# Revit family: 201_RINO-V-_
name_source: partatom
category: Air Terminals
units: mm (PartAtom-declared; Revit-internal decimal feet)

## family parameters
Always vertical = Yes
Cut with Voids When Loaded = No
Part Type = Normal
Room Calculation Point = Yes
Round Connector Dimension = Use Diameter
Shared = No
Work Plane-Based = No

## types (2) — shared parameters
CAT0 = Yes
CL_Location_5000 = 5000 mm  [stored 16.4042 ft]
Description = Supply air device
L_ARR = 400 mm  [stored 1.31234 ft]
Manufacturer = Climecon
QmdConnectorList = 201;D
URL = www.climecon.fi
W_ARR = 400 mm  [stored 1.31234 ft]
XRefLineVPlnId = 7453
YRefLineVPlnId = 7456
magiPartTypeId = 201
magiProductFamilyId = RINO-V-*
zero-valued in all types: CLBTZ, H_ARR, MC_Default_elevation

## per-type parameters (varying)
| type | A1 | A1__ve | AA | D | DL1 | DL1__ve | R | Z1 |
| RINO-V-125 | 231 mm  [stored 0.757874 ft] | -231 mm  [stored -0.757874 ft] | 123 mm  [stored 0.403543 ft] | 125 mm | 193 mm  [stored 0.633202 ft] | -193 mm  [stored -0.633202 ft] | 63 mm | 103 mm |
| RINO-V-160 | 275 mm  [stored 0.902231 ft] | -275 mm  [stored -0.902231 ft] | 147 mm  [stored 0.482283 ft] | 160 mm | 217 mm  [stored 0.711942 ft] | -217 mm  [stored -0.711942 ft] | 80 mm  [stored 0.262467 ft] | 120 mm  [stored 0.393701 ft] |

note: column(s) folded — value = type name in every type: magiProductCode, magiProductId

note: [stored X ft] marks values corroborated as IEEE doubles in the binary element streams (Revit-internal decimal feet)

## geometry (parser evidence)
native form markers: Sweep x2
no freeform markers — native parametric forms only
